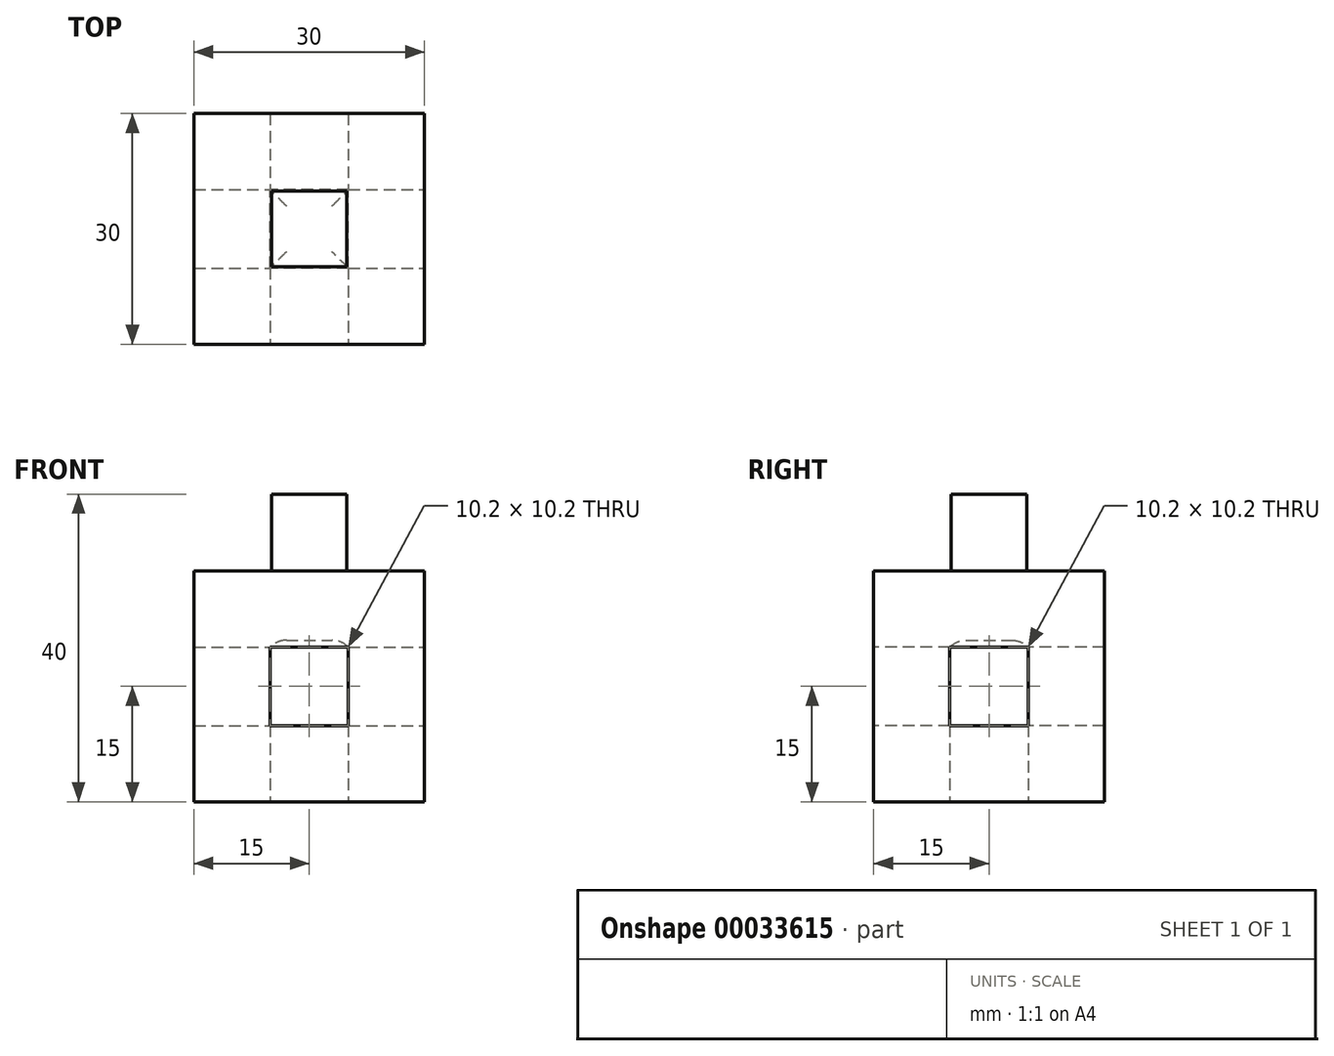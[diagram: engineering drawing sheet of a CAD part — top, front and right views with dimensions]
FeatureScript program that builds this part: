
annotation { "Feature Type Name" : "Feature", "Feature Type Description" : "" }
export const myFeature = defineFeature(function(context is Context, id is Id, definition is map)
    precondition{}
    {
        {
            var Q0;
            Q0=qCreatedBy(makeId("Front.planeOp"),FACE);
            var sketch = newSketch(context, id + "F0", { "sketchPlane" : qUnion([Q0])});
            skLineSegment(sketch, "E0.rect.bottom", {"start": v(15, 15) * mm, "end": v(-15, 15) * mm});
            skLineSegment(sketch, "E0.rect.top", {"start": v(15, -15) * mm, "end": v(-15, -15) * mm});
            skLineSegment(sketch, "E0.rect.left", {"start": v(15, 15) * mm, "end": v(15, -15) * mm});
            skLineSegment(sketch, "E0.rect.right", {"start": v(-15, 15) * mm, "end": v(-15, -15) * mm});
            skPoint(sketch, "E0.rect.middle", {"position": v(0, 0) * mm});
            skSolve(sketch);
        }
        {
            var Q0;
            Q0 = qSketchRegion(id + "F0", true);
            extrude(context, id + "F1", {"entities" : qUnion([Q0]), "endBound" : BoundingType.SYMMETRIC, "depth" : 30 * mm});
        }
        {
            var Q0;
            Q0=makeQuery(id+"F1.opExtrude","SWEPT_FACE",FACE,{"disambiguationData":[OSD([sQuery(id+"F0.wireOp",EDGE,"E0.rect.bottom")])]});
            var sketch = newSketch(context, id + "F2", { "sketchPlane" : qUnion([Q0])});
            skLineSegment(sketch, "E1.rect.bottom", {"start": v(4.9, 4.9) * mm, "end": v(-4.9, 4.9) * mm});
            skLineSegment(sketch, "E1.rect.top", {"start": v(4.9, -4.9) * mm, "end": v(-4.9, -4.9) * mm});
            skLineSegment(sketch, "E1.rect.left", {"start": v(4.9, 4.9) * mm, "end": v(4.9, -4.9) * mm});
            skLineSegment(sketch, "E1.rect.right", {"start": v(-4.9, 4.9) * mm, "end": v(-4.9, -4.9) * mm});
            skPoint(sketch, "E1.rect.middle", {"position": v(0, 0) * mm});
            skSolve(sketch);
        }
        {
            var Q0;
            Q0 = qSketchRegion(id + "F2", true);
            extrude(context, id + "F3", {"entities" : qUnion([Q0]), "operationType" : NewBodyOperationType.ADD, "depth" : 10 * mm});
        }
        {
            var Q0;
            Q0=makeQuery(id+"F1.opExtrude","SWEPT_FACE",FACE,{"disambiguationData":[OSD([sQuery(id+"F0.wireOp",EDGE,"E0.rect.top")])]});
            var sketch = newSketch(context, id + "F4", { "sketchPlane" : qUnion([Q0])});
            skLineSegment(sketch, "E2.rect.bottom", {"start": v(-5.1, 5.1) * mm, "end": v(5.1, 5.1) * mm});
            skLineSegment(sketch, "E2.rect.top", {"start": v(-5.1, -5.1) * mm, "end": v(5.1, -5.1) * mm});
            skLineSegment(sketch, "E2.rect.left", {"start": v(-5.1, 5.1) * mm, "end": v(-5.1, -5.1) * mm});
            skLineSegment(sketch, "E2.rect.right", {"start": v(5.1, 5.1) * mm, "end": v(5.1, -5.1) * mm});
            skPoint(sketch, "E2.rect.middle", {"position": v(0, 0) * mm});
            skSolve(sketch);
        }
        {
            var Q0;
            Q0 = qSketchRegion(id + "F4", true);
            extrude(context, id + "F5", {"entities" : qUnion([Q0]), "operationType" : NewBodyOperationType.REMOVE, "oppositeDirection" : true, "depth" : 21 * mm});
        }
        {
            var Q0;
            Q0=makeQuery(id+"F1.opExtrude","SWEPT_FACE",FACE,{"disambiguationData":[OSD([sQuery(id+"F0.wireOp",EDGE,"E0.rect.left")])]});
            var sketch = newSketch(context, id + "F6", { "sketchPlane" : qUnion([Q0])});
            skLineSegment(sketch, "E3", {"start": v(0, -54.96) * mm, "end": v(0, -15) * mm, "construction": true});
            skPoint(sketch, "E3.endSnap0", {"position": v(0, -15) * mm});
            skLineSegment(sketch, "E4.rect.bottom", {"start": v(-5.1, -5.1) * mm, "end": v(5.1, -5.1) * mm});
            skLineSegment(sketch, "E4.rect.top", {"start": v(-5.1, 5.1) * mm, "end": v(5.1, 5.1) * mm});
            skLineSegment(sketch, "E4.rect.left", {"start": v(-5.1, -5.1) * mm, "end": v(-5.1, 5.1) * mm});
            skLineSegment(sketch, "E4.rect.right", {"start": v(5.1, -5.1) * mm, "end": v(5.1, 5.1) * mm});
            skPoint(sketch, "E4.rect.middle", {"position": v(0, 0) * mm});
            skSolve(sketch);
        }
        {
            var Q0;
            Q0 = qSketchRegion(id + "F6", true);
            extrude(context, id + "F7", {"entities" : qUnion([Q0]), "operationType" : NewBodyOperationType.REMOVE, "oppositeDirection" : true, "depth" : 30 * mm});
        }
        {
            var Q0;
            Q0=makeQuery(id+"F1.opExtrude","CAP_FACE",FACE,{"disambiguationData":[OSD([sQuery(id+"F0.wireOp",EDGE,"E0.rect.bottom"),sQuery(id+"F0.wireOp",EDGE,"E0.rect.top"),sQuery(id+"F0.wireOp",EDGE,"E0.rect.left"),sQuery(id+"F0.wireOp",EDGE,"E0.rect.right")])],"isStart":false});
            var sketch = newSketch(context, id + "F8", { "sketchPlane" : qUnion([Q0])});
            skLineSegment(sketch, "E5", {"start": v(0, -15) * mm, "end": v(0, 15) * mm, "construction": true});
            skPoint(sketch, "E5.endSnap0", {"position": v(0, -15) * mm});
            skLineSegment(sketch, "E6.rect.bottom", {"start": v(-5.1, -5.1) * mm, "end": v(5.1, -5.1) * mm});
            skLineSegment(sketch, "E6.rect.top", {"start": v(-5.1, 5.1) * mm, "end": v(5.1, 5.1) * mm});
            skLineSegment(sketch, "E6.rect.left", {"start": v(-5.1, -5.1) * mm, "end": v(-5.1, 5.1) * mm});
            skLineSegment(sketch, "E6.rect.right", {"start": v(5.1, -5.1) * mm, "end": v(5.1, 5.1) * mm});
            skPoint(sketch, "E6.rect.middle", {"position": v(0, 0) * mm});
            skSolve(sketch);
        }
        {
            var Q0;
            Q0 = qSketchRegion(id + "F8", true);
            extrude(context, id + "F9", {"entities" : qUnion([Q0]), "operationType" : NewBodyOperationType.REMOVE, "endBound" : BoundingType.THROUGH_ALL, "oppositeDirection" : true, "depth" : 25 * mm});
        }
        {
            var Q0;
            Q0=makeQuery(id+"F5.boolean.opBoolean","COPY",EDGE,{"derivedFrom":makeQuery(id+"F5.opExtrude","CAP_EDGE",EDGE,{"disambiguationData":[OSD([sQuery(id+"F4.wireOp",EDGE,"E2.rect.bottom")])],"isStart":false})});
            var Q1;
            Q1=makeQuery(id+"F5.boolean.opBoolean","COPY",EDGE,{"derivedFrom":makeQuery(id+"F5.opExtrude","CAP_EDGE",EDGE,{"disambiguationData":[OSD([sQuery(id+"F4.wireOp",EDGE,"E2.rect.right")])],"isStart":false})});
            var Q2;
            Q2=makeQuery(id+"F5.boolean.opBoolean","COPY",EDGE,{"derivedFrom":makeQuery(id+"F5.opExtrude","CAP_EDGE",EDGE,{"disambiguationData":[OSD([sQuery(id+"F4.wireOp",EDGE,"E2.rect.top")])],"isStart":false})});
            var Q3;
            Q3=makeQuery(id+"F5.boolean.opBoolean","COPY",EDGE,{"derivedFrom":makeQuery(id+"F5.opExtrude","CAP_EDGE",EDGE,{"disambiguationData":[OSD([sQuery(id+"F4.wireOp",EDGE,"E2.rect.left")])],"isStart":false})});
            fillet(context, id + "F10", {"entities" : qUnion([Q0, Q1, Q2, Q3]), "radius" : 3 * mm, "tangentPropagation" : true, "allowEdgeOverflow" : false});
        }
    });
